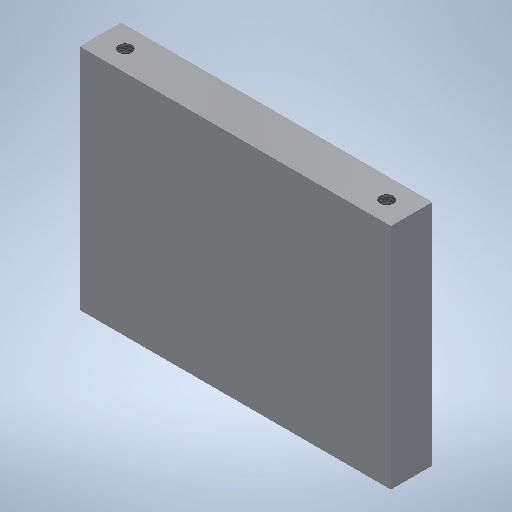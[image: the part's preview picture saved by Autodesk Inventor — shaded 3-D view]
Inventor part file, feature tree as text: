
AUTODESK INVENTOR PART (.ipt)
format: ipt  version: 2025 (Build 290162000, 162)  size: 229,888 bytes
history: native  units: in
note: dims shown in document units (in); Inventor stores cm internally (conversion verified against a paired STEP export)
features: sketch x3, hole x2, extrude x1
ambient origin geometry x8: Origin, YZ Plane, XZ Plane, XY Plane, X Axis, Y Axis, Z Axis, Center Point
bodies: Solid1 (feature_tree)
feature tree (6):
  extrude  "Extrusion1"  Depth=2.9528in
  hole  "Hole2"  [1 undecoded]
  hole  "Hole3"  [1 undecoded]
  sketch  "Sketch1"  dims[d0=2.1654in d1=2.9528in]
  sketch  "Sketch3"  dims[d2=0.3937in d3=0.0in d14=0.2362in]
  sketch  "Sketch4"  dims[d15=0.2362in d16=0.1969in d17=0.1276in d18=0.315in d19=0.375in d20=0.25in d21=0.5635in d22=0.4646in d23=0.8108in d24=0.1969in d25=0.2362in d26=0.2362in d27=0.1276in d28=0.315in d29=0.375in d30=0.25in d31=0.5635in d32=0.4646in d33=0.8108in]
note: 2 required parameter values undecoded (feature->parameter linkage not recoverable at this tier; creation-order binding heuristic only, values carry confidence <= 0.55)
